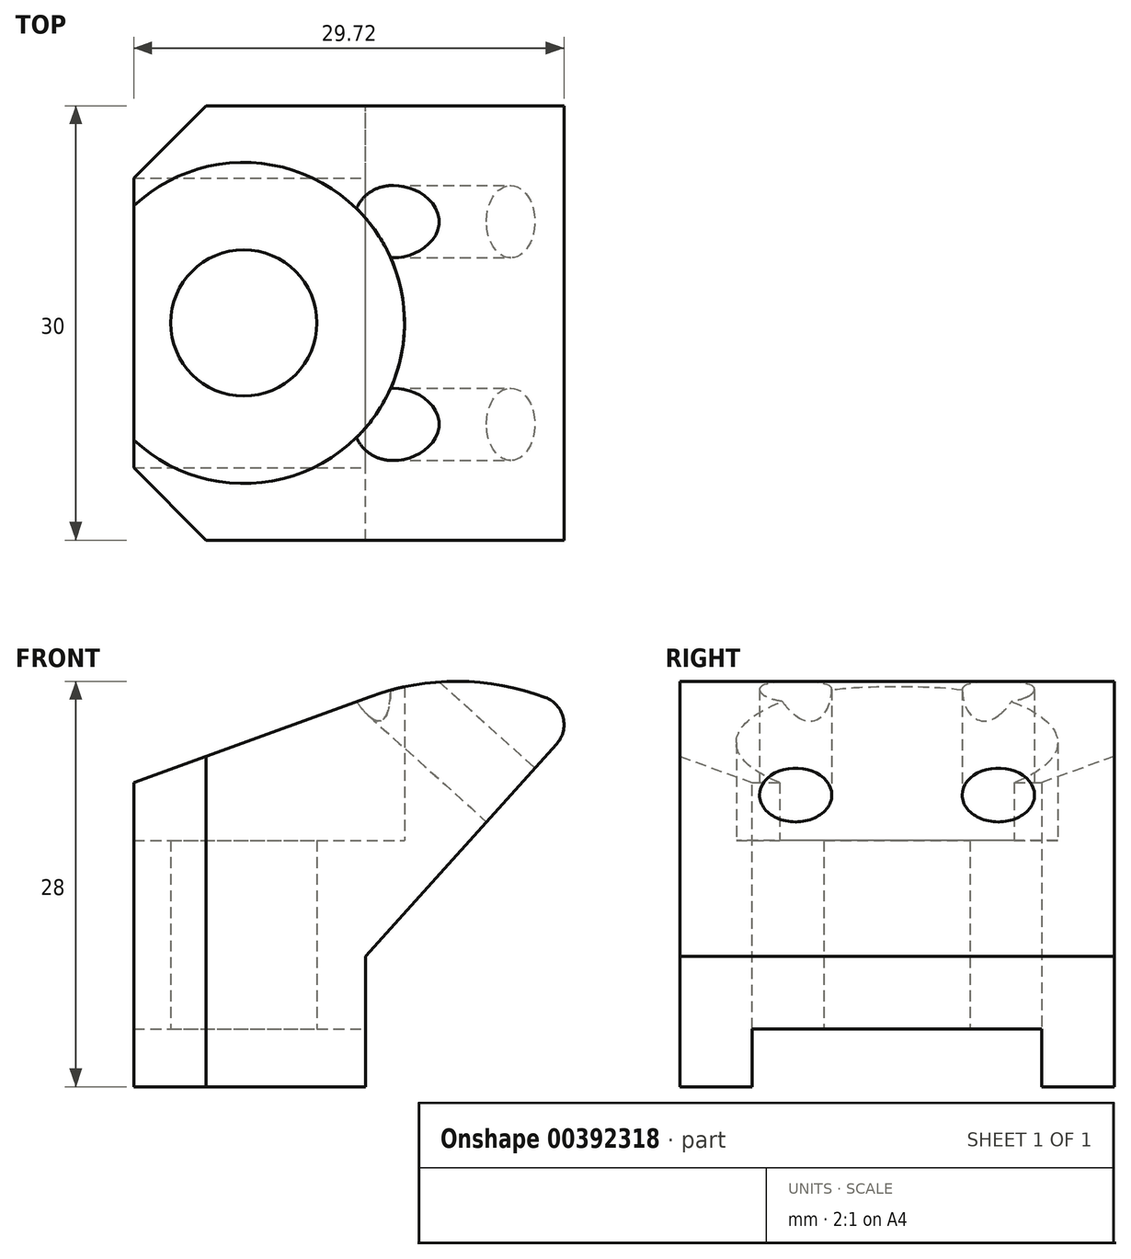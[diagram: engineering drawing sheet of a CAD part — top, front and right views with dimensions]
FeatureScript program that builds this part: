
annotation { "Feature Type Name" : "Feature", "Feature Type Description" : "" }
export const myFeature = defineFeature(function(context is Context, id is Id, definition is map)
    precondition{}
    {
        {
            var Q0;
            Q0=qCreatedBy(makeId("Front.planeOp"),FACE);
            var sketch = newSketch(context, id + "F0", { "sketchPlane" : qUnion([Q0])});
            skLineSegment(sketch, "E0", {"start": v(0, 0) * mm, "end": v(-16, 0) * mm});
            skLineSegment(sketch, "E1", {"start": v(-16, 0) * mm, "end": v(-16, 21) * mm});
            skLineSegment(sketch, "E2", {"start": v(-16, 21) * mm, "end": v(0.36, 26.95) * mm});
            skLineSegment(sketch, "E3", {"start": v(15, 25.66) * mm, "end": v(0, 9) * mm});
            skLineSegment(sketch, "E4", {"start": v(0, 0) * mm, "end": v(0, 9) * mm});
            skLineSegment(sketch, "E5", {"start": v(-8.4, 36.99) * mm, "end": v(-8.4, -12.86) * mm, "construction": true});
            skLineSegment(sketch, "E6.0", {"start": v(2.7, 36.99) * mm, "end": v(2.7, -12.86) * mm, "construction": true});
            skLineSegment(sketch, "E7", {"start": v(-45.02, 28) * mm, "end": v(53.7, 28) * mm, "construction": true});
            skLineSegment(sketch, "E8.0", {"start": v(15, 36.99) * mm, "end": v(15, -12.86) * mm, "construction": true});
            skLineSegment(sketch, "E9.0", {"start": v(-45.02, 25) * mm, "end": v(53.7, 25) * mm, "construction": true});
            skArc(sketch, "E10", {"start": v(15, 25.66) * mm, "mid": v(7.82, 27.93) * mm, "end": v(0.36, 26.95) * mm});
            skSolve(sketch);
        }
        {
            var Q0;
            Q0 = qSketchRegion(id + "F0", true);
            extrude(context, id + "F1", {"entities" : qUnion([Q0]), "depth" : 30 * mm});
        }
        {
            var Q0;
            Q0=makeQuery(id+"F1.opExtrude","SWEPT_FACE",FACE,{"disambiguationData":[OSD([sQuery(id+"F0.wireOp",EDGE,"E0")])]});
            var sketch = newSketch(context, id + "F2", { "sketchPlane" : qUnion([Q0])});
            skLineSegment(sketch, "E11", {"start": v(-8.4, 40.7) * mm, "end": v(-8.4, -5.57) * mm, "construction": true});
            skLineSegment(sketch, "E12", {"start": v(-26.35, 15) * mm, "end": v(26.47, 15) * mm, "construction": true});
            skPoint(sketch, "E13.orphan", {"position": v(-16, 15) * mm});
            skCircle(sketch, "E14", {"center": v(-8.4, 15) * mm, "radius": 5.05 * mm});
            skCircle(sketch, "E15", {"center": v(-8.4, 15) * mm, "radius": 11 * mm});
            skSolve(sketch);
        }
        {
            var Q0;
            Q0=makeQuery(id+"F2.imprint","IMPRINT",FACE,{"disambiguationData":[TD([[makeQuery(id+"F2.imprint","IMPRINT",EDGE,{"derivedFrom":sQuery(id+"F2.wireOp",EDGE,"E14")}),1.0]])]});
            extrude(context, id + "F3", {"entities" : qUnion([Q0]), "operationType" : NewBodyOperationType.REMOVE, "endBound" : BoundingType.THROUGH_ALL, "oppositeDirection" : true, "depth" : 25 * mm});
        }
        {
            var Q0;
            Q0=makeQuery(id+"F1.opExtrude","SWEPT_FACE",FACE,{"disambiguationData":[OSD([sQuery(id+"F0.wireOp",EDGE,"E0")])]});
            var sketch = newSketch(context, id + "F4", { "sketchPlane" : qUnion([Q0])});
            skLineSegment(sketch, "E16", {"start": v(-16, 5) * mm, "end": v(0, 5) * mm});
            skLineSegment(sketch, "E17.0", {"start": v(-16, 25) * mm, "end": v(0, 25) * mm});
            skSolve(sketch);
        }
        {
            var Q0;
            {var subQ0=sQuery(id+"F4.wireOp",EDGE,"E16");Q0=makeQuery(id+"F4.imprint","IMPRINT",FACE,{"disambiguationData":[TD([[makeQuery(id+"F4.imprint","IMPRINT",EDGE,{"derivedFrom":subQ0}),1.0]])]});}
            extrude(context, id + "F5", {"entities" : qUnion([Q0]), "operationType" : NewBodyOperationType.REMOVE, "oppositeDirection" : true, "depth" : 4 * mm});
        }
        {
            var Q0;
            Q0=makeQuery(id+"F5.boolean.opBoolean","COPY",FACE,{"derivedFrom":makeQuery(id+"F5.opExtrude","CAP_FACE",FACE,{"disambiguationData":[OSD([sQuery(id+"F0.wireOp",EDGE,"E0"),sQuery(id+"F0.wireOp",EDGE,"E1"),sQuery(id+"F0.wireOp",EDGE,"E4"),sQuery(id+"F2.wireOp",EDGE,"E14"),sQuery(id+"F4.wireOp",EDGE,"E16"),sQuery(id+"F4.wireOp",EDGE,"E17.0")])],"isStart":false})});
            cPlane(context, id + "F6", {"entities" : qUnion([Q0]), "cplaneType" : CPlaneType.OFFSET, "offset" : 13 * mm, "oppositeDirection" : true, "width" : 150 * mm, "height" : 150 * mm});
        }
        {
            var Q0;
            Q0=qCreatedBy(id+"F6.planeOp",FACE);
            var sketch = newSketch(context, id + "F7", { "sketchPlane" : qUnion([Q0])});
            skCircle(sketch, "E18", {"center": v(-8.4, 15) * mm, "radius": 11.1 * mm});
            skSolve(sketch);
        }
        {
            var Q0;
            Q0=makeQuery(id+"F7.imprint","IMPRINT",FACE,{"disambiguationData":[TD([[makeQuery(id+"F7.imprint","IMPRINT",EDGE,{"derivedFrom":sQuery(id+"F7.wireOp",EDGE,"E18")}),1.0]])]});
            var Q1;
            Q1=sQuery(id+"F7.wireOp",EDGE,"E18");
            extrude(context, id + "F8", {"entities" : qUnion([Q0]), "operationType" : NewBodyOperationType.REMOVE, "surfaceEntities" : qUnion([Q1]), "endBound" : BoundingType.THROUGH_ALL, "oppositeDirection" : true, "depth" : 25 * mm});
        }
        {
            var Q0;
            Q0=makeQuery(id+"F1.opExtrude","CAP_EDGE",EDGE,{"disambiguationData":[OSD([sQuery(id+"F0.wireOp",EDGE,"E1")])],"isStart":false});
            var Q1;
            Q1=makeQuery(id+"F1.opExtrude","CAP_EDGE",EDGE,{"disambiguationData":[OSD([sQuery(id+"F0.wireOp",EDGE,"E1")])],"isStart":true});
            chamfer(context, id + "F9", {"entities" : qUnion([Q0, Q1]), "width" : 5 * mm, "tangentPropagation" : true});
        }
        {
            var Q0;
            Q0=makeQuery(id+"F1.opExtrude","SWEPT_EDGE",EDGE,{"disambiguationData":[OSD([sQuery(id+"F0.wireOp",EDGE,"E3"),sQuery(id+"F0.wireOp",EDGE,"E10")])]});
            fillet(context, id + "F10", {"entities" : qUnion([Q0]), "radius" : 2 * mm, "tangentPropagation" : true, "allowEdgeOverflow" : false});
        }
        {
            var Q0;
            Q0=makeQuery(id+"F1.opExtrude","SWEPT_FACE",FACE,{"disambiguationData":[OSD([sQuery(id+"F0.wireOp",EDGE,"E3")])]});
            var sketch = newSketch(context, id + "F11", { "sketchPlane" : qUnion([Q0])});
            skLineSegment(sketch, "E19", {"start": v(-69.4, 21.69) * mm, "end": v(39.2, 21.69) * mm, "construction": true});
            skLineSegment(sketch, "E20", {"start": v(-22, -23.68) * mm, "end": v(-22, 38.85) * mm, "construction": true});
            skLineSegment(sketch, "E21.0", {"start": v(-8, -23.68) * mm, "end": v(-8, 38.85) * mm, "construction": true});
            skCircle(sketch, "E22", {"center": v(-22, 21.69) * mm, "radius": 2.5 * mm});
            skPoint(sketch, "E23.endSnap0", {"position": v(-15, 6.69) * mm});
            skCircle(sketch, "E24.MirrorC", {"center": v(-8, 21.69) * mm, "radius": 2.5 * mm});
            skSolve(sketch);
        }
        {
            var Q0;
            Q0 = qSketchRegion(id + "F11", true);
            extrude(context, id + "F12", {"entities" : qUnion([Q0]), "operationType" : NewBodyOperationType.REMOVE, "endBound" : BoundingType.THROUGH_ALL, "oppositeDirection" : true, "depth" : 25 * mm});
        }
    });
